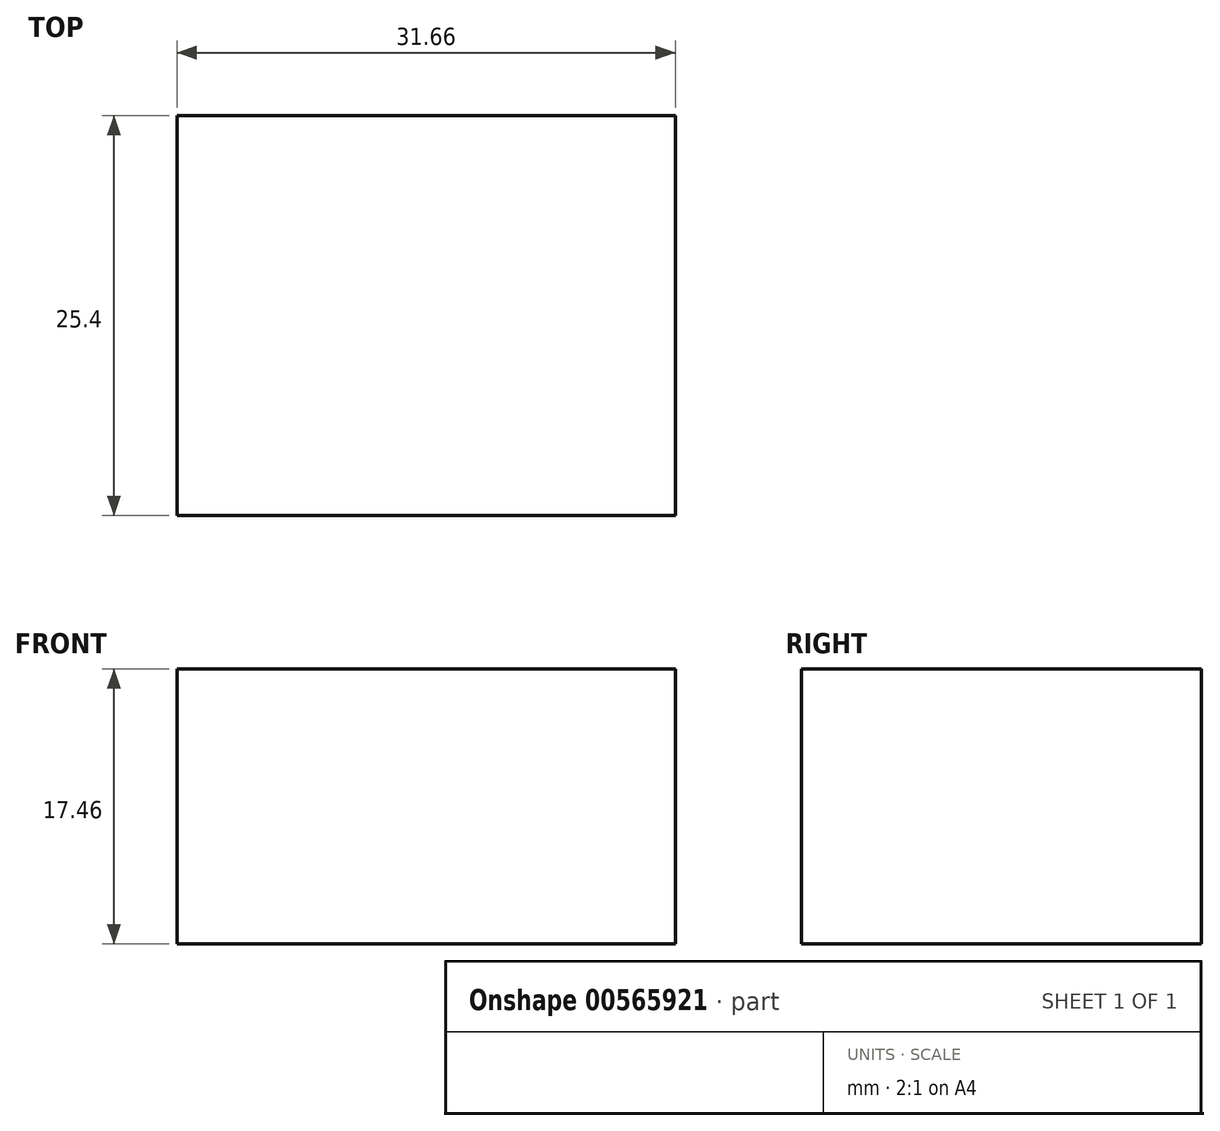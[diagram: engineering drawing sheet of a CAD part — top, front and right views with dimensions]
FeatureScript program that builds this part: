
annotation { "Feature Type Name" : "Feature", "Feature Type Description" : "" }
export const myFeature = defineFeature(function(context is Context, id is Id, definition is map)
    precondition{}
    {
        {
            var Q0;
            Q0=qCreatedBy(makeId("Front.planeOp"),FACE);
            var sketch = newSketch(context, id + "F0", { "sketchPlane" : qUnion([Q0])});
            skLineSegment(sketch, "E0.bottom", {"start": v(0, 0) * mm, "end": v(31.66, 0) * mm});
            skLineSegment(sketch, "E0.top", {"start": v(0, 17.46) * mm, "end": v(31.66, 17.46) * mm});
            skLineSegment(sketch, "E0.left", {"start": v(0, 0) * mm, "end": v(0, 17.46) * mm});
            skLineSegment(sketch, "E0.right", {"start": v(31.66, 0) * mm, "end": v(31.66, 17.46) * mm});
            skSolve(sketch);
        }
        {
            var Q0;
            Q0 = qSketchRegion(id + "F0", true);
            extrude(context, id + "F1", {"entities" : qUnion([Q0]), "oppositeDirection" : true, "depth" : 25.4 * mm, "offsetDistance" : 25.4 * mm});
        }
    });
